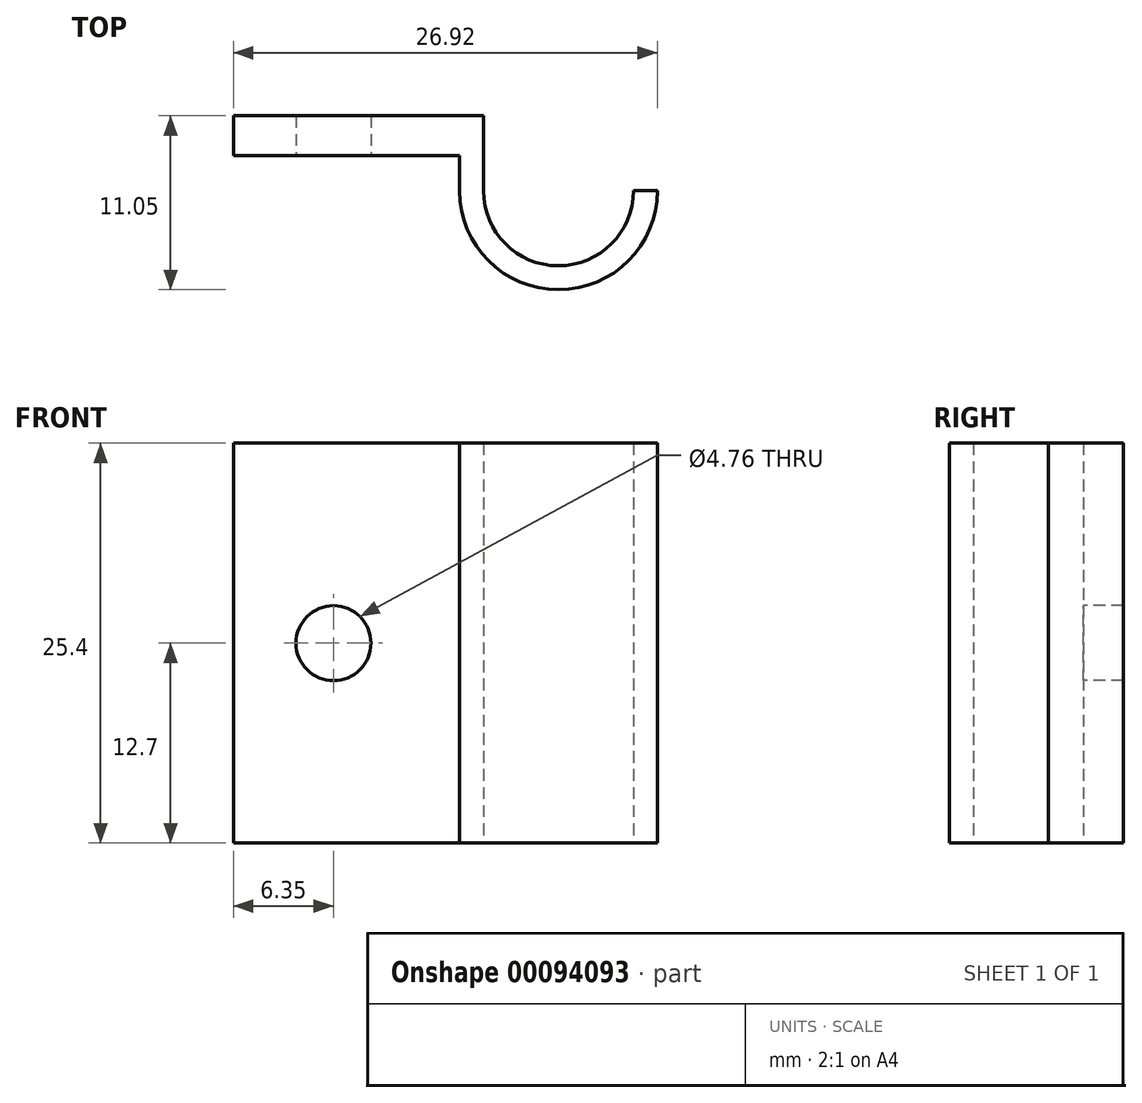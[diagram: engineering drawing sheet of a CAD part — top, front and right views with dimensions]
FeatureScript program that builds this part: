
annotation { "Feature Type Name" : "Feature", "Feature Type Description" : "" }
export const myFeature = defineFeature(function(context is Context, id is Id, definition is map)
    precondition{}
    {
        {
            var Q0;
            Q0=qCreatedBy(makeId("Top.planeOp"),FACE);
            var sketch = newSketch(context, id + "F0", { "sketchPlane" : qUnion([Q0])});
            skLineSegment(sketch, "E0.bottom", {"start": v(0, 0) * mm, "end": v(15.88, 0) * mm});
            skLineSegment(sketch, "E0.top", {"start": v(0, -2.54) * mm, "end": v(15.88, -2.54) * mm});
            skLineSegment(sketch, "E0.left", {"start": v(0, 0) * mm, "end": v(0, -2.54) * mm});
            skLineSegment(sketch, "E0.right", {"start": v(15.88, 0) * mm, "end": v(15.88, -2.54) * mm});
            skLineSegment(sketch, "E1.bottom", {"start": v(15.88, 0) * mm, "end": v(14.35, 0) * mm});
            skLineSegment(sketch, "E1.top", {"start": v(15.88, -4.76) * mm, "end": v(14.35, -4.76) * mm});
            skLineSegment(sketch, "E1.left", {"start": v(15.88, 0) * mm, "end": v(15.88, -4.76) * mm});
            skLineSegment(sketch, "E1.right", {"start": v(14.35, 0) * mm, "end": v(14.35, -4.76) * mm});
            skArc(sketch, "E2", {"start": v(14.35, -4.76) * mm, "mid": v(20.64, -11.05) * mm, "end": v(26.92, -4.76) * mm});
            skArc(sketch, "E3", {"start": v(15.88, -4.76) * mm, "mid": v(20.64, -9.52) * mm, "end": v(25.4, -4.76) * mm});
            skLineSegment(sketch, "E4", {"start": v(25.4, -4.76) * mm, "end": v(26.92, -4.76) * mm});
            skSolve(sketch);
        }
        {
            var Q0;
            {var subQ0=sQuery(id+"F0.wireOp",EDGE,"E0.bottom");Q0=makeQuery(id+"F0.imprint","IMPRINT",FACE,{"disambiguationData":[TD([[makeQuery(id+"F0.imprint","IMPRINT",EDGE,{"derivedFrom":subQ0}),-1.0]])]});}
            var Q1;
            {var subQ5=sQuery(id+"F0.wireOp",EDGE,"E1.bottom");Q1=makeQuery(id+"F0.imprint","IMPRINT",FACE,{"disambiguationData":[TD([[makeQuery(id+"F0.imprint","IMPRINT",EDGE,{"derivedFrom":subQ5}),1.0]])]});}
            var Q2;
            {var subQ5=sQuery(id+"F0.wireOp",EDGE,"E1.top");Q2=makeQuery(id+"F0.imprint","IMPRINT",FACE,{"disambiguationData":[TD([[makeQuery(id+"F0.imprint","IMPRINT",EDGE,{"derivedFrom":subQ5}),-1.0]])]});}
            var Q3;
            Q3=makeQuery(id+"F0.imprint","IMPRINT",FACE,{"disambiguationData":[TD([[makeQuery(id+"F0.imprint","IMPRINT",EDGE,{"derivedFrom":sQuery(id+"F0.wireOp",EDGE,"E1.top")}),1.0]])]});
            extrude(context, id + "F1", {"entities" : qUnion([Q0, Q1, Q2, Q3]), "depth" : 25.4 * mm, "offsetDistance" : 25.4 * mm});
        }
        {
            var Q0;
            Q0=makeQuery(id+"F1.opExtrude","SWEPT_FACE",FACE,{"disambiguationData":[OSD([sQuery(id+"F0.wireOp",EDGE,"E0.top")])]});
            var sketch = newSketch(context, id + "F2", { "sketchPlane" : qUnion([Q0])});
            skLineSegment(sketch, "E5", {"start": v(0, 12.7) * mm, "end": v(6.35, 12.7) * mm});
            skCircle(sketch, "E6", {"center": v(6.35, 12.7) * mm, "radius": 2.38 * mm});
            skSolve(sketch);
        }
        {
            var Q0;
            Q0=makeQuery(id+"F2.imprint","IMPRINT",FACE,{"disambiguationData":[TD([[makeQuery(id+"F2.imprint","IMPRINT",EDGE,{"derivedFrom":sQuery(id+"F2.wireOp",EDGE,"E6")}),1.0]])]});
            extrude(context, id + "F3", {"entities" : qUnion([Q0]), "operationType" : NewBodyOperationType.REMOVE, "oppositeDirection" : true, "depth" : 25.4 * mm, "offsetDistance" : 25.4 * mm});
        }
    });
